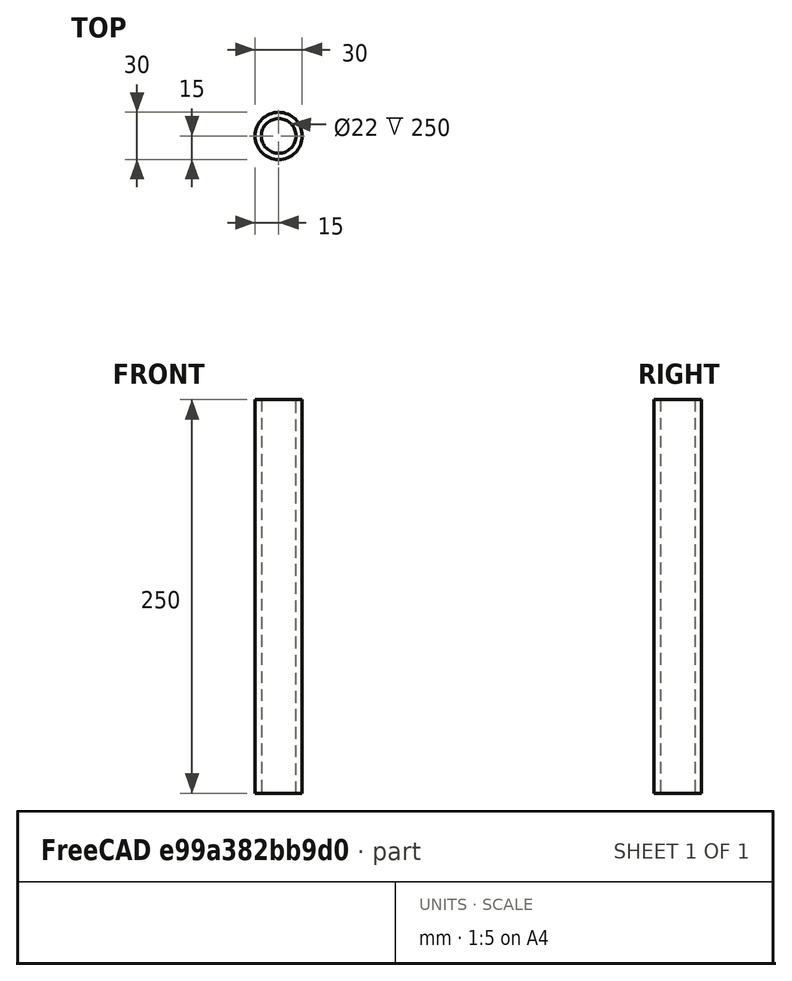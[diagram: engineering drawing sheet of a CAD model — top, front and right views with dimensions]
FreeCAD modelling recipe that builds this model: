
FCSTD DOCUMENT  (FreeCAD 0.19R24267 +99 (Git))
Label: Albero-Mandrino
License: All rights reserved
LicenseURL: http://en.wikipedia.org/wiki/All_rights_reserved
objects: Sketcher::SketchObject×1, PartDesign::Pad×1, PartDesign::Body×1
note: 4 computed .brp shape members not serialized (recipe doc carries the construction recipe); baked Part::Feature solids carry a one-line shape summary decoded from their .brp

FEATURE [Sketcher::SketchObject] Sketch
  FullyConstrained = true
  MapMode = 5
  Support = -> [XY_Plane]
  sketch-geometry (2):
    g0: Circle CenterX=0 CenterY=0 CenterZ=0 NormalX=0 NormalY=0 NormalZ=1 AngleXU=0 Radius=15
    g1: Circle CenterX=0 CenterY=0 CenterZ=0 NormalX=0 NormalY=0 NormalZ=1 AngleXU=0 Radius=11
  constraints (4):
    c: Coincident(g0,g-1)
    c: Radius(g0) = 15
    c: Coincident(g1,g0)
    c: Radius(g1) = 11
FEATURE [PartDesign::Pad] Pad
  Direction = (1,1,1)
  Length = 250
  Length2 = 100
  Profile = -> Sketch
  Type = 0
FEATURE [PartDesign::Body] Body
  Group = -> [Sketch,Pad]
  Origin = -> Origin
  Tip = -> Pad
